# Revit family: Hive Work Surface - Fan
name_source: partatom
category: Furniture
units: mm (PartAtom-declared; Revit-internal decimal feet)

## family parameters
Always vertical = Yes
Cut with Voids When Loaded = No
OmniClass Number = 23.40.20.00
OmniClass Title = General Furniture and Specialties
Room Calculation Point = No
Shared = Yes
Work Plane-Based = No

## types (1)
- Hive Work Surface - Fan
    AssetIdentifier = THV8
    Barcode = 0
    COBie Description = Designed by Roger Webb Associates, Hive is designed to create flexible spaces for collaboration, communication and concentration. A versatile modular system which integrates technology
    Default Elevation = 0' - 0"
    Depth = 2' - 11 7/16"
    Description = Fan Work Surface
    Height = 2' - 5 1/8"
    Length = 2' - 7 1/2"
    Manufacturer = Palmer Hamilton
    Model = THV8
    Name = Furniture -Table-Casual-Connection-Hive_Fan_Work_Surface
    Product Code = THV8
    Product URL = http://www.nomadflexiblefurniture.com
    SerialNumber = 0
    TagNumber = 0
    Type Comments = Fan Work Surface
    URL = http://www.nomadflexiblefurniture.com
    Uniclass = Pr_40_50_21
    WarrantyDuration = 60

## geometry (parser evidence)
native form markers: Blend x2, Sweep x6
no freeform markers — native parametric forms only
